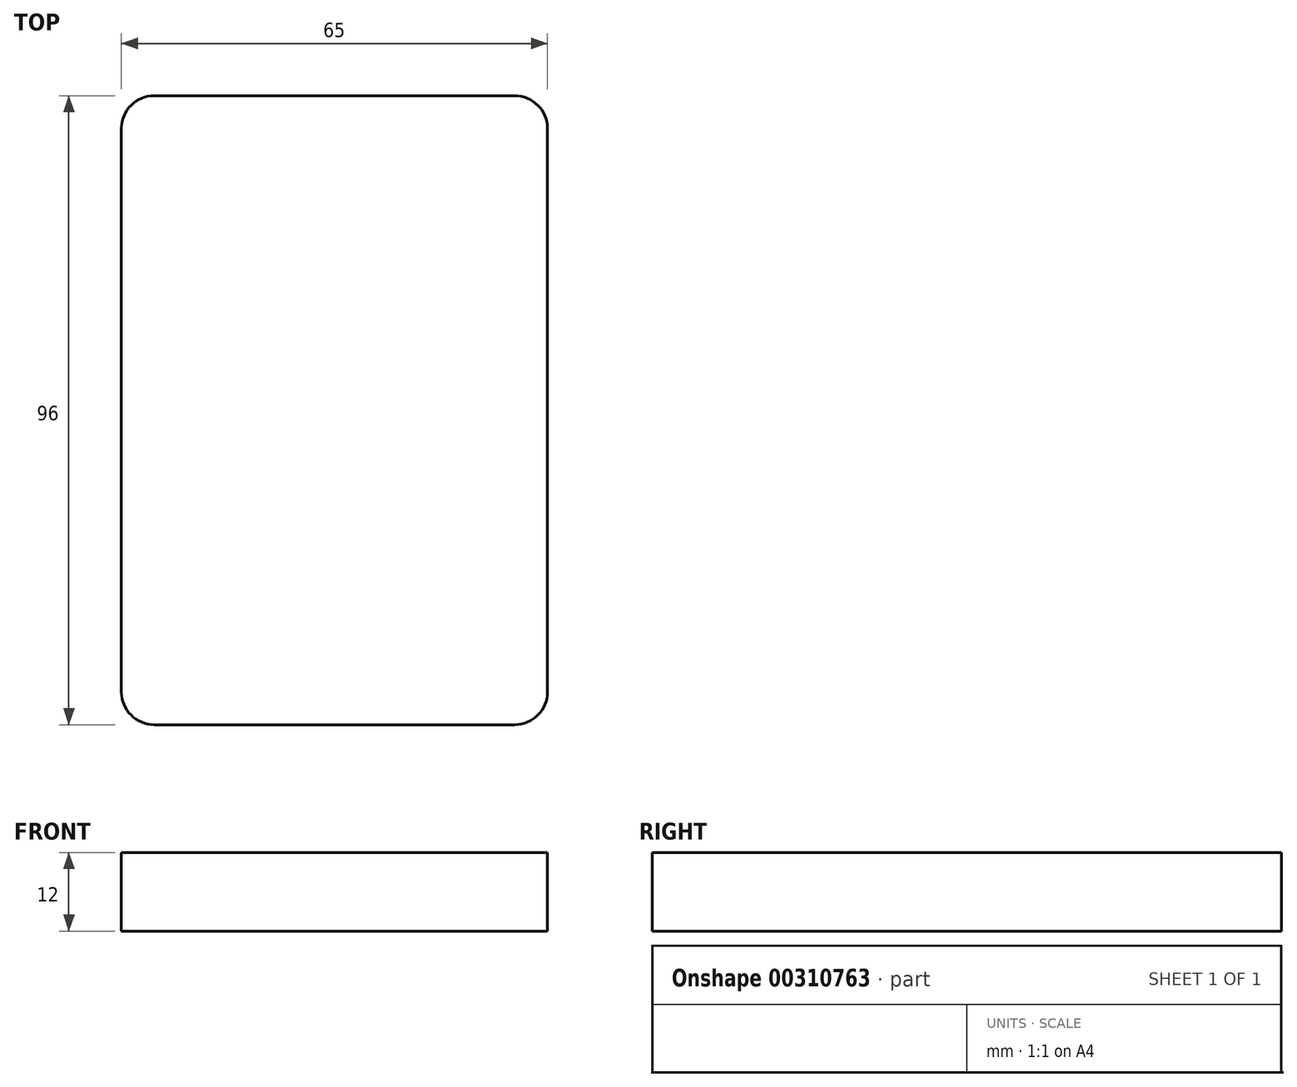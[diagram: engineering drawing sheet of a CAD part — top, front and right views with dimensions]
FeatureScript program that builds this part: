
annotation { "Feature Type Name" : "Feature", "Feature Type Description" : "" }
export const myFeature = defineFeature(function(context is Context, id is Id, definition is map)
    precondition{}
    {
        {
            var Q0;
            Q0=qCreatedBy(makeId("Top.planeOp"),FACE);
            var sketch = newSketch(context, id + "F0", { "sketchPlane" : qUnion([Q0])});
            skLineSegment(sketch, "E0", {"start": v(-51.67, 43.8) * mm, "end": v(-51.67, -52.2) * mm});
            skLineSegment(sketch, "E1", {"start": v(-51.67, -52.2) * mm, "end": v(13.33, -52.2) * mm});
            skLineSegment(sketch, "E2", {"start": v(13.33, -52.2) * mm, "end": v(13.33, 43.8) * mm});
            skLineSegment(sketch, "E3", {"start": v(13.33, 43.8) * mm, "end": v(-51.67, 43.8) * mm});
            skSolve(sketch);
        }
        {
            var Q0;
            Q0 = qSketchRegion(id + "F0", true);
            extrude(context, id + "F1", {"entities" : qUnion([Q0]), "depth" : 12 * mm});
        }
        {
            var Q0;
            Q0=makeQuery(id+"F1.opExtrude","SWEPT_EDGE",EDGE,{"disambiguationData":[OSD([sQuery(id+"F0.wireOp",EDGE,"E0"),sQuery(id+"F0.wireOp",EDGE,"E3")])]});
            var Q1;
            Q1=makeQuery(id+"F1.opExtrude","SWEPT_EDGE",EDGE,{"disambiguationData":[OSD([sQuery(id+"F0.wireOp",EDGE,"E2"),sQuery(id+"F0.wireOp",EDGE,"E3")])]});
            var Q2;
            Q2=makeQuery(id+"F1.opExtrude","SWEPT_EDGE",EDGE,{"disambiguationData":[OSD([sQuery(id+"F0.wireOp",EDGE,"E1"),sQuery(id+"F0.wireOp",EDGE,"E2")])]});
            var Q3;
            Q3=makeQuery(id+"F1.opExtrude","SWEPT_EDGE",EDGE,{"disambiguationData":[OSD([sQuery(id+"F0.wireOp",EDGE,"E0"),sQuery(id+"F0.wireOp",EDGE,"E1")])]});
            fillet(context, id + "F2", {"entities" : qUnion([Q0, Q1, Q2, Q3]), "radius" : 5 * mm, "tangentPropagation" : true, "allowEdgeOverflow" : false});
        }
    });
